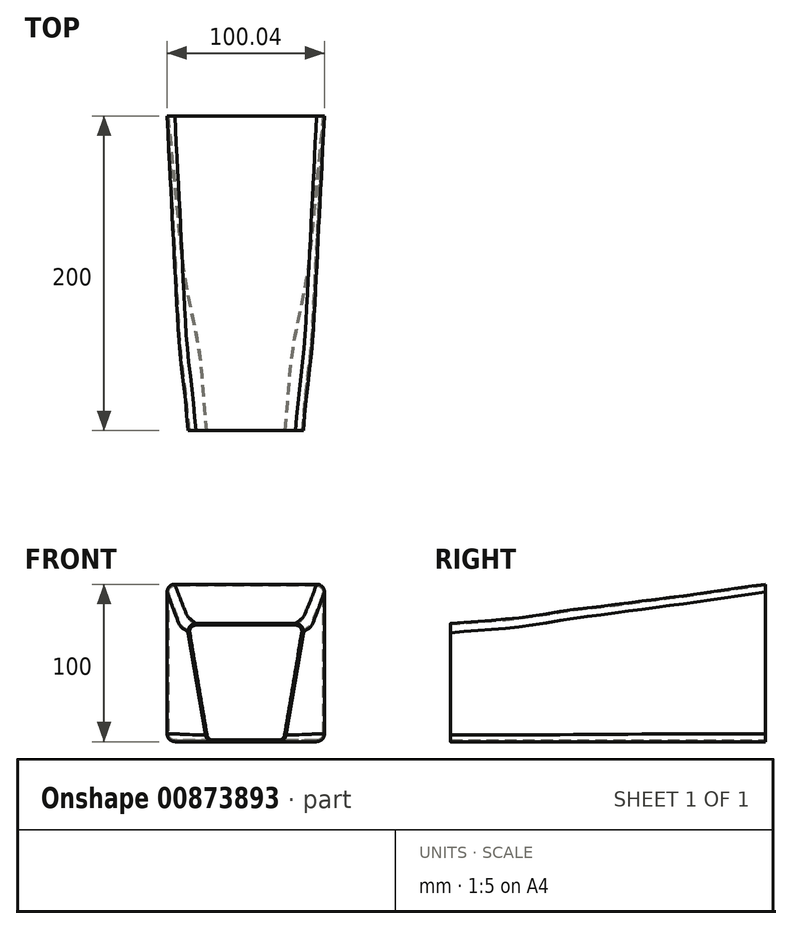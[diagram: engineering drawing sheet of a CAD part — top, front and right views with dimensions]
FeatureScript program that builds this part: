
annotation { "Feature Type Name" : "Feature", "Feature Type Description" : "" }
export const myFeature = defineFeature(function(context is Context, id is Id, definition is map)
    precondition{}
    {
        {
            var Q0;
            Q0=qCreatedBy(makeId("Front.planeOp"),FACE);
            cPlane(context, id + "F0", {"entities" : qUnion([Q0]), "cplaneType" : CPlaneType.OFFSET, "offset" : 25 * mm, "width" : 150 * mm, "height" : 150 * mm});
        }
        {
            var Q0;
            Q0=qCreatedBy(makeId("Front.planeOp"),FACE);
            cPlane(context, id + "F1", {"entities" : qUnion([Q0]), "cplaneType" : CPlaneType.OFFSET, "offset" : 50 * mm, "width" : 150 * mm, "height" : 150 * mm});
        }
        {
            var Q0;
            Q0=qCreatedBy(makeId("Front.planeOp"),FACE);
            cPlane(context, id + "F2", {"entities" : qUnion([Q0]), "cplaneType" : CPlaneType.OFFSET, "offset" : 75 * mm, "width" : 150 * mm, "height" : 150 * mm});
        }
        {
            var Q0;
            Q0=qCreatedBy(makeId("Front.planeOp"),FACE);
            cPlane(context, id + "F3", {"entities" : qUnion([Q0]), "cplaneType" : CPlaneType.OFFSET, "offset" : 100 * mm, "width" : 150 * mm, "height" : 150 * mm});
        }
        {
            var Q0;
            Q0=qCreatedBy(makeId("Front.planeOp"),FACE);
            cPlane(context, id + "F4", {"entities" : qUnion([Q0]), "cplaneType" : CPlaneType.OFFSET, "offset" : 125 * mm, "width" : 150 * mm, "height" : 150 * mm});
        }
        {
            var Q0;
            Q0=qCreatedBy(makeId("Front.planeOp"),FACE);
            cPlane(context, id + "F5", {"entities" : qUnion([Q0]), "cplaneType" : CPlaneType.OFFSET, "offset" : 150 * mm, "width" : 150 * mm, "height" : 150 * mm});
        }
        {
            var Q0;
            Q0=qCreatedBy(makeId("Front.planeOp"),FACE);
            cPlane(context, id + "F6", {"entities" : qUnion([Q0]), "cplaneType" : CPlaneType.OFFSET, "offset" : 175 * mm, "width" : 150 * mm, "height" : 150 * mm});
        }
        {
            var Q0;
            Q0=qCreatedBy(makeId("Front.planeOp"),FACE);
            cPlane(context, id + "F7", {"entities" : qUnion([Q0]), "cplaneType" : CPlaneType.OFFSET, "offset" : 200 * mm, "width" : 150 * mm, "height" : 150 * mm});
        }
        {
            var Q0;
            Q0=qCreatedBy(makeId("Front.planeOp"),FACE);
            var sketch = newSketch(context, id + "F8", { "sketchPlane" : qUnion([Q0])});
            skLineSegment(sketch, "E0.bottom", {"start": v(50, -50) * mm, "end": v(-50, -50) * mm});
            skLineSegment(sketch, "E0.top", {"start": v(50, 50) * mm, "end": v(-50, 50) * mm});
            skLineSegment(sketch, "E0.left", {"start": v(50, -50) * mm, "end": v(50, 50) * mm});
            skLineSegment(sketch, "E0.right", {"start": v(-50, -50) * mm, "end": v(-50, 50) * mm});
            skPoint(sketch, "E0.middle", {"position": v(0, 0) * mm});
            skSolve(sketch);
        }
        {
            var Q0;
            Q0=qCreatedBy(id+"F7.planeOp",FACE);
            var sketch = newSketch(context, id + "F9", { "sketchPlane" : qUnion([Q0])});
            skLineSegment(sketch, "E1.0.0", {"start": v(50, -50) * mm, "end": v(50, 50) * mm, "construction": true});
            skLineSegment(sketch, "E1.0.1", {"start": v(50, 50) * mm, "end": v(-50, 50) * mm, "construction": true});
            skLineSegment(sketch, "E1.0.2", {"start": v(-50, 50) * mm, "end": v(-50, -50) * mm, "construction": true});
            skLineSegment(sketch, "E1.0.3", {"start": v(-50, -50) * mm, "end": v(50, -50) * mm, "construction": true});
            skLineSegment(sketch, "E2", {"start": v(-25, -50) * mm, "end": v(25, -50) * mm});
            skLineSegment(sketch, "E3", {"start": v(25, -50) * mm, "end": v(37.5, 25) * mm});
            skLineSegment(sketch, "E4", {"start": v(37.5, 25) * mm, "end": v(-37.5, 25) * mm});
            skLineSegment(sketch, "E5", {"start": v(-37.5, 25) * mm, "end": v(-25, -50) * mm});
            skPoint(sketch, "E6", {"position": v(0, 25) * mm});
            skSolve(sketch);
        }
        {
            var Q0;
            Q0=qCreatedBy(id+"F6.planeOp",FACE);
            var sketch = newSketch(context, id + "F10", { "sketchPlane" : qUnion([Q0])});
            skLineSegment(sketch, "E7.0.0", {"start": v(37.5, 25) * mm, "end": v(-37.5, 25) * mm, "construction": true});
            skLineSegment(sketch, "E7.0.1", {"start": v(-37.5, 25) * mm, "end": v(-25, -50) * mm, "construction": true});
            skLineSegment(sketch, "E7.0.2", {"start": v(-25, -50) * mm, "end": v(25, -50) * mm, "construction": true});
            skLineSegment(sketch, "E7.0.3", {"start": v(25, -50) * mm, "end": v(37.5, 25) * mm, "construction": true});
            skLineSegment(sketch, "E8.0.0", {"start": v(50, -50) * mm, "end": v(50, 50) * mm, "construction": true});
            skLineSegment(sketch, "E8.0.1", {"start": v(50, 50) * mm, "end": v(-50, 50) * mm, "construction": true});
            skLineSegment(sketch, "E8.0.2", {"start": v(-50, 50) * mm, "end": v(-50, -50) * mm, "construction": true});
            skLineSegment(sketch, "E8.0.3", {"start": v(-50, -50) * mm, "end": v(50, -50) * mm, "construction": true});
            skLineSegment(sketch, "E9", {"start": v(-27, -50) * mm, "end": v(27, -50) * mm});
            skLineSegment(sketch, "E10", {"start": v(27, -50) * mm, "end": v(39.83, 27) * mm});
            skLineSegment(sketch, "E11", {"start": v(39.83, 27) * mm, "end": v(-39.83, 27) * mm});
            skLineSegment(sketch, "E12", {"start": v(-39.83, 27) * mm, "end": v(-27, -50) * mm});
            skPoint(sketch, "E13", {"position": v(0, 27) * mm});
            skPoint(sketch, "E14", {"position": v(0, -50) * mm});
            skPoint(sketch, "E15", {"position": v(0, 25) * mm});
            skSolve(sketch);
        }
        {
            var Q0;
            Q0=qCreatedBy(id+"F5.planeOp",FACE);
            var sketch = newSketch(context, id + "F11", { "sketchPlane" : qUnion([Q0])});
            skLineSegment(sketch, "E16.0.0", {"start": v(50, -50) * mm, "end": v(50, 50) * mm, "construction": true});
            skLineSegment(sketch, "E16.0.1", {"start": v(50, 50) * mm, "end": v(-50, 50) * mm, "construction": true});
            skLineSegment(sketch, "E16.0.2", {"start": v(-50, 50) * mm, "end": v(-50, -50) * mm, "construction": true});
            skLineSegment(sketch, "E16.0.3", {"start": v(-50, -50) * mm, "end": v(50, -50) * mm, "construction": true});
            skLineSegment(sketch, "E17.0.0", {"start": v(39.83, 27) * mm, "end": v(-39.83, 27) * mm, "construction": true});
            skLineSegment(sketch, "E17.0.1", {"start": v(-39.83, 27) * mm, "end": v(-27, -50) * mm, "construction": true});
            skLineSegment(sketch, "E17.0.2", {"start": v(-27, -50) * mm, "end": v(27, -50) * mm, "construction": true});
            skLineSegment(sketch, "E17.0.3", {"start": v(27, -50) * mm, "end": v(39.83, 27) * mm, "construction": true});
            skLineSegment(sketch, "E18", {"start": v(-29.5, -50) * mm, "end": v(29.5, -50) * mm});
            skLineSegment(sketch, "E19", {"start": v(29.5, -50) * mm, "end": v(42.75, 29.5) * mm});
            skLineSegment(sketch, "E20", {"start": v(42.75, 29.5) * mm, "end": v(-42.75, 29.5) * mm});
            skLineSegment(sketch, "E21", {"start": v(-42.75, 29.5) * mm, "end": v(-29.5, -50) * mm});
            skPoint(sketch, "E22", {"position": v(0, 29.5) * mm});
            skPoint(sketch, "E23", {"position": v(0, -50) * mm});
            skSolve(sketch);
        }
        {
            var Q0;
            Q0=qCreatedBy(id+"F4.planeOp",FACE);
            var sketch = newSketch(context, id + "F12", { "sketchPlane" : qUnion([Q0])});
            skLineSegment(sketch, "E24.0.0", {"start": v(50, -50) * mm, "end": v(50, 50) * mm, "construction": true});
            skLineSegment(sketch, "E24.0.1", {"start": v(50, 50) * mm, "end": v(-50, 50) * mm, "construction": true});
            skLineSegment(sketch, "E24.0.2", {"start": v(-50, 50) * mm, "end": v(-50, -50) * mm, "construction": true});
            skLineSegment(sketch, "E24.0.3", {"start": v(-50, -50) * mm, "end": v(50, -50) * mm, "construction": true});
            skLineSegment(sketch, "E25.0.0", {"start": v(42.75, 29.5) * mm, "end": v(-42.75, 29.5) * mm, "construction": true});
            skLineSegment(sketch, "E25.0.1", {"start": v(-42.75, 29.5) * mm, "end": v(-29.5, -50) * mm, "construction": true});
            skLineSegment(sketch, "E25.0.2", {"start": v(-29.5, -50) * mm, "end": v(29.5, -50) * mm, "construction": true});
            skLineSegment(sketch, "E25.0.3", {"start": v(29.5, -50) * mm, "end": v(42.75, 29.5) * mm, "construction": true});
            skLineSegment(sketch, "E26", {"start": v(42.75, 29.5) * mm, "end": v(50, 50) * mm, "construction": true});
            skLineSegment(sketch, "E27", {"start": v(-42.75, 29.5) * mm, "end": v(-50, 50) * mm, "construction": true});
            skLineSegment(sketch, "E28", {"start": v(-34.5, -50) * mm, "end": v(-44.16, 33.5) * mm});
            skLineSegment(sketch, "E29", {"start": v(-44.16, 33.5) * mm, "end": v(44.16, 33.5) * mm});
            skLineSegment(sketch, "E30", {"start": v(44.16, 33.5) * mm, "end": v(34.5, -50) * mm});
            skLineSegment(sketch, "E31", {"start": v(34.5, -50) * mm, "end": v(-34.5, -50) * mm});
            skPoint(sketch, "E32", {"position": v(0, -50) * mm});
            skSolve(sketch);
        }
        {
            var Q0;
            Q0=qCreatedBy(id+"F3.planeOp",FACE);
            var sketch = newSketch(context, id + "F13", { "sketchPlane" : qUnion([Q0])});
            skLineSegment(sketch, "E33.0.0", {"start": v(50, -50) * mm, "end": v(50, 50) * mm, "construction": true});
            skLineSegment(sketch, "E33.0.1", {"start": v(50, 50) * mm, "end": v(-50, 50) * mm, "construction": true});
            skLineSegment(sketch, "E33.0.2", {"start": v(-50, 50) * mm, "end": v(-50, -50) * mm, "construction": true});
            skLineSegment(sketch, "E33.0.3", {"start": v(-50, -50) * mm, "end": v(50, -50) * mm, "construction": true});
            skLineSegment(sketch, "E34.0.0", {"start": v(-34.5, -50) * mm, "end": v(34.5, -50) * mm, "construction": true});
            skLineSegment(sketch, "E34.0.1", {"start": v(34.5, -50) * mm, "end": v(44.16, 33.5) * mm, "construction": true});
            skLineSegment(sketch, "E34.0.2", {"start": v(44.16, 33.5) * mm, "end": v(-44.16, 33.5) * mm, "construction": true});
            skLineSegment(sketch, "E34.0.3", {"start": v(-44.16, 33.5) * mm, "end": v(-34.5, -50) * mm, "construction": true});
            skLineSegment(sketch, "E35", {"start": v(-44.16, 33.5) * mm, "end": v(-50, 50) * mm, "construction": true});
            skLineSegment(sketch, "E36", {"start": v(44.16, 33.5) * mm, "end": v(50, 50) * mm, "construction": true});
            skLineSegment(sketch, "E37", {"start": v(-39.5, -50) * mm, "end": v(-45.23, 36.5) * mm});
            skLineSegment(sketch, "E38", {"start": v(-45.23, 36.5) * mm, "end": v(45.23, 36.5) * mm});
            skLineSegment(sketch, "E39", {"start": v(45.23, 36.5) * mm, "end": v(39.5, -50) * mm});
            skLineSegment(sketch, "E40", {"start": v(39.5, -50) * mm, "end": v(-39.5, -50) * mm});
            skPoint(sketch, "E41", {"position": v(0, -50) * mm});
            skSolve(sketch);
        }
        {
            var Q0;
            Q0=qCreatedBy(id+"F2.planeOp",FACE);
            var sketch = newSketch(context, id + "F14", { "sketchPlane" : qUnion([Q0])});
            skLineSegment(sketch, "E42.0.0", {"start": v(50, -50) * mm, "end": v(50, 50) * mm, "construction": true});
            skLineSegment(sketch, "E42.0.1", {"start": v(50, 50) * mm, "end": v(-50, 50) * mm, "construction": true});
            skLineSegment(sketch, "E42.0.2", {"start": v(-50, 50) * mm, "end": v(-50, -50) * mm, "construction": true});
            skLineSegment(sketch, "E42.0.3", {"start": v(-50, -50) * mm, "end": v(50, -50) * mm, "construction": true});
            skLineSegment(sketch, "E43.0.0", {"start": v(-39.5, -50) * mm, "end": v(39.5, -50) * mm, "construction": true});
            skLineSegment(sketch, "E43.0.1", {"start": v(39.5, -50) * mm, "end": v(45.23, 36.5) * mm, "construction": true});
            skLineSegment(sketch, "E43.0.2", {"start": v(45.23, 36.5) * mm, "end": v(-45.23, 36.5) * mm, "construction": true});
            skLineSegment(sketch, "E43.0.3", {"start": v(-45.23, 36.5) * mm, "end": v(-39.5, -50) * mm, "construction": true});
            skLineSegment(sketch, "E44", {"start": v(-45.23, 36.5) * mm, "end": v(-50, 50) * mm, "construction": true});
            skLineSegment(sketch, "E45", {"start": v(45.23, 36.5) * mm, "end": v(50, 50) * mm, "construction": true});
            skLineSegment(sketch, "E46", {"start": v(-42.5, -50) * mm, "end": v(-46.37, 39.75) * mm});
            skLineSegment(sketch, "E47", {"start": v(-46.37, 39.75) * mm, "end": v(46.37, 39.75) * mm});
            skLineSegment(sketch, "E48", {"start": v(46.37, 39.75) * mm, "end": v(42.5, -50) * mm});
            skLineSegment(sketch, "E49", {"start": v(42.5, -50) * mm, "end": v(-42.5, -50) * mm});
            skPoint(sketch, "E50", {"position": v(0, -50) * mm});
            skSolve(sketch);
        }
        {
            var Q0;
            Q0=qCreatedBy(id+"F1.planeOp",FACE);
            var sketch = newSketch(context, id + "F15", { "sketchPlane" : qUnion([Q0])});
            skLineSegment(sketch, "E51.0.0", {"start": v(50, -50) * mm, "end": v(50, 50) * mm, "construction": true});
            skLineSegment(sketch, "E51.0.1", {"start": v(50, 50) * mm, "end": v(-50, 50) * mm, "construction": true});
            skLineSegment(sketch, "E51.0.2", {"start": v(-50, 50) * mm, "end": v(-50, -50) * mm, "construction": true});
            skLineSegment(sketch, "E51.0.3", {"start": v(-50, -50) * mm, "end": v(50, -50) * mm, "construction": true});
            skLineSegment(sketch, "E52.0.0", {"start": v(-42.5, -50) * mm, "end": v(42.5, -50) * mm, "construction": true});
            skLineSegment(sketch, "E52.0.1", {"start": v(42.5, -50) * mm, "end": v(46.37, 39.75) * mm, "construction": true});
            skLineSegment(sketch, "E52.0.2", {"start": v(46.37, 39.75) * mm, "end": v(-46.37, 39.75) * mm, "construction": true});
            skLineSegment(sketch, "E52.0.3", {"start": v(-46.37, 39.75) * mm, "end": v(-42.5, -50) * mm, "construction": true});
            skLineSegment(sketch, "E53", {"start": v(-46.37, 39.75) * mm, "end": v(-50, 50) * mm, "construction": true});
            skLineSegment(sketch, "E54", {"start": v(46.37, 39.75) * mm, "end": v(50, 50) * mm, "construction": true});
            skLineSegment(sketch, "E55", {"start": v(-45, -50) * mm, "end": v(-47.52, 43) * mm});
            skLineSegment(sketch, "E56", {"start": v(-47.52, 43) * mm, "end": v(47.52, 43) * mm});
            skLineSegment(sketch, "E57", {"start": v(47.52, 43) * mm, "end": v(45, -50) * mm});
            skLineSegment(sketch, "E58", {"start": v(45, -50) * mm, "end": v(-45, -50) * mm});
            skPoint(sketch, "E59", {"position": v(0, -50) * mm});
            skSolve(sketch);
        }
        {
            var Q0;
            Q0=qCreatedBy(id+"F0.planeOp",FACE);
            var sketch = newSketch(context, id + "F16", { "sketchPlane" : qUnion([Q0])});
            skLineSegment(sketch, "E60.0.0", {"start": v(50, -50) * mm, "end": v(50, 50) * mm, "construction": true});
            skLineSegment(sketch, "E60.0.1", {"start": v(50, 50) * mm, "end": v(-50, 50) * mm, "construction": true});
            skLineSegment(sketch, "E60.0.2", {"start": v(-50, 50) * mm, "end": v(-50, -50) * mm, "construction": true});
            skLineSegment(sketch, "E60.0.3", {"start": v(-50, -50) * mm, "end": v(50, -50) * mm, "construction": true});
            skLineSegment(sketch, "E61.0.0", {"start": v(-45, -50) * mm, "end": v(45, -50) * mm, "construction": true});
            skLineSegment(sketch, "E61.0.1", {"start": v(45, -50) * mm, "end": v(47.52, 43) * mm, "construction": true});
            skLineSegment(sketch, "E61.0.2", {"start": v(47.52, 43) * mm, "end": v(-47.52, 43) * mm, "construction": true});
            skLineSegment(sketch, "E61.0.3", {"start": v(-47.52, 43) * mm, "end": v(-45, -50) * mm, "construction": true});
            skLineSegment(sketch, "E62", {"start": v(-47.52, 43) * mm, "end": v(-50, 50) * mm, "construction": true});
            skLineSegment(sketch, "E63", {"start": v(47.52, 43) * mm, "end": v(50, 50) * mm, "construction": true});
            skLineSegment(sketch, "E64", {"start": v(-47.5, -50) * mm, "end": v(47.5, -50) * mm});
            skLineSegment(sketch, "E65", {"start": v(47.5, -50) * mm, "end": v(48.76, 46.5) * mm});
            skLineSegment(sketch, "E66", {"start": v(48.76, 46.5) * mm, "end": v(-48.76, 46.5) * mm});
            skLineSegment(sketch, "E67", {"start": v(-48.76, 46.5) * mm, "end": v(-47.5, -50) * mm});
            skPoint(sketch, "E68", {"position": v(0, -50) * mm});
            skSolve(sketch);
        }
        {
            var Q0;
            Q0=makeQuery(id+"F8.imprint","IMPRINT",FACE,{"disambiguationData":[TD([[makeQuery(id+"F8.imprint","IMPRINT",EDGE,{"derivedFrom":sQuery(id+"F8.wireOp",EDGE,"E0.bottom")}),-1.0]])]});
            var Q1;
            Q1=makeQuery(id+"F16.imprint","IMPRINT",FACE,{"disambiguationData":[TD([[makeQuery(id+"F16.imprint","IMPRINT",EDGE,{"derivedFrom":sQuery(id+"F16.wireOp",EDGE,"E64")}),1.0]])]});
            var Q2;
            Q2=makeQuery(id+"F15.imprint","IMPRINT",FACE,{"disambiguationData":[TD([[makeQuery(id+"F15.imprint","IMPRINT",EDGE,{"derivedFrom":sQuery(id+"F15.wireOp",EDGE,"E55")}),-1.0]])]});
            var Q3;
            Q3=makeQuery(id+"F14.imprint","IMPRINT",FACE,{"disambiguationData":[TD([[makeQuery(id+"F14.imprint","IMPRINT",EDGE,{"derivedFrom":sQuery(id+"F14.wireOp",EDGE,"E46")}),-1.0]])]});
            var Q4;
            Q4=makeQuery(id+"F13.imprint","IMPRINT",FACE,{"disambiguationData":[TD([[makeQuery(id+"F13.imprint","IMPRINT",EDGE,{"derivedFrom":sQuery(id+"F13.wireOp",EDGE,"E37")}),-1.0]])]});
            var Q5;
            Q5=makeQuery(id+"F12.imprint","IMPRINT",FACE,{"disambiguationData":[TD([[makeQuery(id+"F12.imprint","IMPRINT",EDGE,{"derivedFrom":sQuery(id+"F12.wireOp",EDGE,"E28")}),-1.0]])]});
            var Q6;
            Q6=makeQuery(id+"F11.imprint","IMPRINT",FACE,{"disambiguationData":[TD([[makeQuery(id+"F11.imprint","IMPRINT",EDGE,{"derivedFrom":sQuery(id+"F11.wireOp",EDGE,"E18")}),1.0]])]});
            var Q7;
            Q7=makeQuery(id+"F10.imprint","IMPRINT",FACE,{"disambiguationData":[TD([[makeQuery(id+"F10.imprint","IMPRINT",EDGE,{"derivedFrom":sQuery(id+"F10.wireOp",EDGE,"E9")}),1.0]])]});
            var Q8;
            Q8=makeQuery(id+"F9.imprint","IMPRINT",FACE,{"disambiguationData":[TD([[makeQuery(id+"F9.imprint","IMPRINT",EDGE,{"derivedFrom":sQuery(id+"F9.wireOp",EDGE,"E2")}),1.0]])]});
            loft(context, id + "F17", {"sheetProfilesArray" : [{ "sheetProfileEntities" : qUnion([Q0]) }, { "sheetProfileEntities" : qUnion([Q1]) }, { "sheetProfileEntities" : qUnion([Q2]) }, { "sheetProfileEntities" : qUnion([Q3]) }, { "sheetProfileEntities" : qUnion([Q4]) }, { "sheetProfileEntities" : qUnion([Q5]) }, { "sheetProfileEntities" : qUnion([Q6]) }, { "sheetProfileEntities" : qUnion([Q7]) }, { "sheetProfileEntities" : qUnion([Q8]) }]});
        }
        {
            var Q0;
            Q0=makeQuery(id+"F17.opLoft","SWEPT_EDGE",EDGE,{"disambiguationData":[OSD([sQuery(id+"F8.wireOp",EDGE,"E0.top"),sQuery(id+"F8.wireOp",EDGE,"E0.left"),sQuery(id+"F9.wireOp",EDGE,"E3"),sQuery(id+"F9.wireOp",EDGE,"E4"),sQuery(id+"F10.wireOp",EDGE,"E10"),sQuery(id+"F10.wireOp",EDGE,"E11"),sQuery(id+"F11.wireOp",EDGE,"E19"),sQuery(id+"F11.wireOp",EDGE,"E20"),sQuery(id+"F12.wireOp",EDGE,"E29"),sQuery(id+"F12.wireOp",EDGE,"E30"),sQuery(id+"F13.wireOp",EDGE,"E38"),sQuery(id+"F13.wireOp",EDGE,"E39"),sQuery(id+"F14.wireOp",EDGE,"E47"),sQuery(id+"F14.wireOp",EDGE,"E48"),sQuery(id+"F15.wireOp",EDGE,"E56"),sQuery(id+"F15.wireOp",EDGE,"E57"),sQuery(id+"F16.wireOp",EDGE,"E65"),sQuery(id+"F16.wireOp",EDGE,"E66")])]});
            var Q1;
            Q1=makeQuery(id+"F17.opLoft","SWEPT_EDGE",EDGE,{"disambiguationData":[OSD([sQuery(id+"F8.wireOp",EDGE,"E0.bottom"),sQuery(id+"F8.wireOp",EDGE,"E0.left"),sQuery(id+"F9.wireOp",EDGE,"E2"),sQuery(id+"F9.wireOp",EDGE,"E3"),sQuery(id+"F10.wireOp",EDGE,"E9"),sQuery(id+"F10.wireOp",EDGE,"E10"),sQuery(id+"F11.wireOp",EDGE,"E18"),sQuery(id+"F11.wireOp",EDGE,"E19"),sQuery(id+"F12.wireOp",EDGE,"E30"),sQuery(id+"F12.wireOp",EDGE,"E31"),sQuery(id+"F13.wireOp",EDGE,"E39"),sQuery(id+"F13.wireOp",EDGE,"E40"),sQuery(id+"F14.wireOp",EDGE,"E48"),sQuery(id+"F14.wireOp",EDGE,"E49"),sQuery(id+"F15.wireOp",EDGE,"E57"),sQuery(id+"F15.wireOp",EDGE,"E58"),sQuery(id+"F16.wireOp",EDGE,"E64"),sQuery(id+"F16.wireOp",EDGE,"E65")])]});
            var Q2;
            Q2=makeQuery(id+"F17.opLoft","SWEPT_EDGE",EDGE,{"disambiguationData":[OSD([sQuery(id+"F8.wireOp",EDGE,"E0.top"),sQuery(id+"F8.wireOp",EDGE,"E0.right"),sQuery(id+"F9.wireOp",EDGE,"E4"),sQuery(id+"F9.wireOp",EDGE,"E5"),sQuery(id+"F10.wireOp",EDGE,"E11"),sQuery(id+"F10.wireOp",EDGE,"E12"),sQuery(id+"F11.wireOp",EDGE,"E20"),sQuery(id+"F11.wireOp",EDGE,"E21"),sQuery(id+"F12.wireOp",EDGE,"E28"),sQuery(id+"F12.wireOp",EDGE,"E29"),sQuery(id+"F13.wireOp",EDGE,"E37"),sQuery(id+"F13.wireOp",EDGE,"E38"),sQuery(id+"F14.wireOp",EDGE,"E46"),sQuery(id+"F14.wireOp",EDGE,"E47"),sQuery(id+"F15.wireOp",EDGE,"E55"),sQuery(id+"F15.wireOp",EDGE,"E56"),sQuery(id+"F16.wireOp",EDGE,"E66"),sQuery(id+"F16.wireOp",EDGE,"E67")])]});
            var Q3;
            Q3=makeQuery(id+"F17.opLoft","SWEPT_EDGE",EDGE,{"disambiguationData":[OSD([sQuery(id+"F8.wireOp",EDGE,"E0.bottom"),sQuery(id+"F8.wireOp",EDGE,"E0.right"),sQuery(id+"F9.wireOp",EDGE,"E2"),sQuery(id+"F9.wireOp",EDGE,"E5"),sQuery(id+"F10.wireOp",EDGE,"E9"),sQuery(id+"F10.wireOp",EDGE,"E12"),sQuery(id+"F11.wireOp",EDGE,"E18"),sQuery(id+"F11.wireOp",EDGE,"E21"),sQuery(id+"F12.wireOp",EDGE,"E28"),sQuery(id+"F12.wireOp",EDGE,"E31"),sQuery(id+"F13.wireOp",EDGE,"E37"),sQuery(id+"F13.wireOp",EDGE,"E40"),sQuery(id+"F14.wireOp",EDGE,"E46"),sQuery(id+"F14.wireOp",EDGE,"E49"),sQuery(id+"F15.wireOp",EDGE,"E55"),sQuery(id+"F15.wireOp",EDGE,"E58"),sQuery(id+"F16.wireOp",EDGE,"E64"),sQuery(id+"F16.wireOp",EDGE,"E67")])]});
            fillet(context, id + "F18", {"entities" : qUnion([Q0, Q1, Q2, Q3]), "radius" : 5 * mm, "tangentPropagation" : true, "allowEdgeOverflow" : false});
        }
        {
            var Q0;
            Q0=makeQuery(id+"F17.opLoft","CAP_FACE",FACE,{"disambiguationData":[OSD([makeQuery(id+"F9.imprint","IMPRINT",FACE,{"disambiguationData":[TD([[makeQuery(id+"F9.imprint","IMPRINT",EDGE,{"derivedFrom":sQuery(id+"F9.wireOp",EDGE,"E2")}),1.0]])]})])],"isStart":true});
            var Q1;
            Q1=makeQuery(id+"F17.opLoft","CAP_FACE",FACE,{"disambiguationData":[OSD([makeQuery(id+"F8.imprint","IMPRINT",FACE,{"disambiguationData":[TD([[makeQuery(id+"F8.imprint","IMPRINT",EDGE,{"derivedFrom":sQuery(id+"F8.wireOp",EDGE,"E0.bottom")}),-1.0]])]})])],"isStart":true});
            shell(context, id + "F19", {"entities" : qUnion([Q0, Q1]), "thickness" : 1 * mm});
        }
    });
